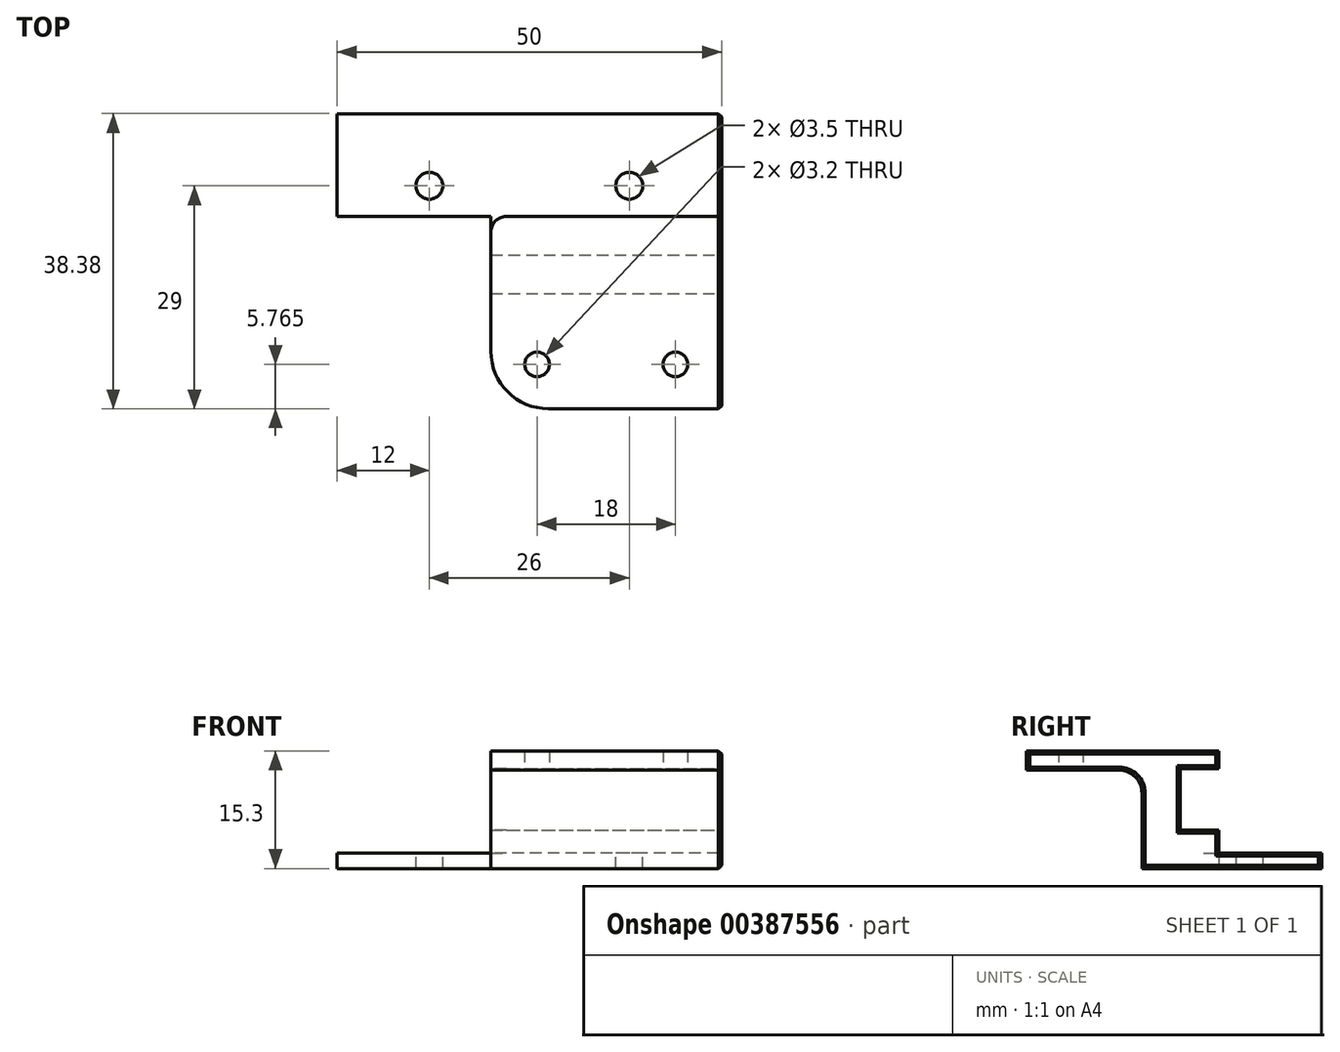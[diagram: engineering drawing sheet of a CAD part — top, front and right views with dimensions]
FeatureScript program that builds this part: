
annotation { "Feature Type Name" : "Feature", "Feature Type Description" : "" }
export const myFeature = defineFeature(function(context is Context, id is Id, definition is map)
    precondition{}
    {
        {
            var Q0;
            Q0=qCreatedBy(makeId("Right.planeOp"),FACE);
            var sketch = newSketch(context, id + "F0", { "sketchPlane" : qUnion([Q0])});
            skLineSegment(sketch, "E0", {"start": v(0, 0) * mm, "end": v(13.38, 0) * mm});
            skLineSegment(sketch, "E1", {"start": v(13.38, 0) * mm, "end": v(13.38, 2) * mm});
            skLineSegment(sketch, "E2", {"start": v(13.38, 2) * mm, "end": v(0, 2) * mm});
            skLineSegment(sketch, "E3", {"start": v(0, 2) * mm, "end": v(0, 0) * mm});
            skSolve(sketch);
        }
        {
            var Q0;
            Q0=makeQuery(id+"F0.imprint","IMPRINT",FACE,{"disambiguationData":[TD([[makeQuery(id+"F0.imprint","IMPRINT",EDGE,{"derivedFrom":sQuery(id+"F0.wireOp",EDGE,"E0")}),1.0]])]});
            extrude(context, id + "F1", {"entities" : qUnion([Q0]), "endBound" : BoundingType.SYMMETRIC, "depth" : 50 * mm});
        }
        {
            var Q0;
            Q0=makeQuery(id+"F1.opExtrude","SWEPT_FACE",FACE,{"disambiguationData":[OSD([sQuery(id+"F0.wireOp",EDGE,"E2")])]});
            var sketch = newSketch(context, id + "F2", { "sketchPlane" : qUnion([Q0])});
            skLineSegment(sketch, "E4", {"start": v(-25, 4) * mm, "end": v(25, 4) * mm, "construction": true});
            skLineSegment(sketch, "E5", {"start": v(0, 13.38) * mm, "end": v(0, 0) * mm, "construction": true});
            skCircle(sketch, "E6", {"center": v(-13, 4) * mm, "radius": 1.75 * mm});
            skCircle(sketch, "E7", {"center": v(13, 4) * mm, "radius": 1.75 * mm});
            skSolve(sketch);
        }
        {
            var Q0;
            Q0=qSketchRegion(id+"F2",true);
            extrude(context, id + "F3", {"entities" : qUnion([Q0]), "operationType" : NewBodyOperationType.REMOVE, "endBound" : BoundingType.UP_TO_NEXT, "oppositeDirection" : true, "depth" : 25 * mm});
        }
        {
            var Q0;
            Q0=makeQuery(id+"F1.opExtrude","CAP_FACE",FACE,{"disambiguationData":[OSD([sQuery(id+"F0.wireOp",EDGE,"E0"),sQuery(id+"F0.wireOp",EDGE,"E1"),sQuery(id+"F0.wireOp",EDGE,"E2"),sQuery(id+"F0.wireOp",EDGE,"E3")])],"isStart":false});
            var sketch = newSketch(context, id + "F4", { "sketchPlane" : qUnion([Q0])});
            skLineSegment(sketch, "E8", {"start": v(0, 0) * mm, "end": v(0, 15.3) * mm});
            skLineSegment(sketch, "E9", {"start": v(0, 15.3) * mm, "end": v(-25, 15.3) * mm});
            skLineSegment(sketch, "E10", {"start": v(-25, 15.3) * mm, "end": v(-25, 12.8) * mm});
            skLineSegment(sketch, "E11", {"start": v(-25, 12.8) * mm, "end": v(-10, 12.8) * mm});
            skLineSegment(sketch, "E12", {"start": v(-10, 12.8) * mm, "end": v(-10, 0) * mm});
            skLineSegment(sketch, "E13", {"start": v(-10, 0) * mm, "end": v(0, 0) * mm});
            skSolve(sketch);
        }
        {
            var Q0;
            Q0=qSketchRegion(id+"F4",true);
            extrude(context, id + "F5", {"entities" : qUnion([Q0]), "operationType" : NewBodyOperationType.ADD, "oppositeDirection" : true, "depth" : 30 * mm});
        }
        {
            var Q0;
            Q0=makeQuery(id+"F5.boolean.opBoolean","MERGE",FACE,{"derivedFrom":[makeQuery(id+"F1.opExtrude","CAP_FACE",FACE,{"disambiguationData":[OSD([sQuery(id+"F0.wireOp",EDGE,"E0"),sQuery(id+"F0.wireOp",EDGE,"E1"),sQuery(id+"F0.wireOp",EDGE,"E2"),sQuery(id+"F0.wireOp",EDGE,"E3")])],"isStart":false}),makeQuery(id+"F5.opExtrude","CAP_FACE",FACE,{"disambiguationData":[OSD([sQuery(id+"F4.wireOp",EDGE,"E8"),sQuery(id+"F4.wireOp",EDGE,"E9"),sQuery(id+"F4.wireOp",EDGE,"E10"),sQuery(id+"F4.wireOp",EDGE,"E11"),sQuery(id+"F4.wireOp",EDGE,"E12"),sQuery(id+"F4.wireOp",EDGE,"E13")])],"isStart":true})]});
            var sketch = newSketch(context, id + "F6", { "sketchPlane" : qUnion([Q0])});
            skLineSegment(sketch, "E14.bottom", {"start": v(0, 5) * mm, "end": v(-5, 5) * mm});
            skLineSegment(sketch, "E14.top", {"start": v(0, 13) * mm, "end": v(-5, 13) * mm});
            skLineSegment(sketch, "E14.left", {"start": v(0, 5) * mm, "end": v(0, 13) * mm});
            skLineSegment(sketch, "E14.right", {"start": v(-5, 5) * mm, "end": v(-5, 13) * mm});
            skSolve(sketch);
        }
        {
            var Q0;
            Q0=qSketchRegion(id+"F6",true);
            extrude(context, id + "F7", {"entities" : qUnion([Q0]), "operationType" : NewBodyOperationType.REMOVE, "endBound" : BoundingType.THROUGH_ALL, "oppositeDirection" : true, "depth" : 25 * mm});
        }
        {
            var Q0;
            Q0=makeQuery(id+"F5.opExtrude","SWEPT_FACE",FACE,{"disambiguationData":[OSD([sQuery(id+"F4.wireOp",EDGE,"E11")])]});
            var sketch = newSketch(context, id + "F8", { "sketchPlane" : qUnion([Q0])});
            skLineSegment(sketch, "E15", {"start": v(7, 25) * mm, "end": v(13, 25) * mm});
            skLineSegment(sketch, "E16", {"start": v(13, 25) * mm, "end": v(20.04, 23.1) * mm});
            skLineSegment(sketch, "E17", {"start": v(20.04, 15.37) * mm, "end": v(13, 13.47) * mm});
            skLineSegment(sketch, "E18", {"start": v(13, 13.47) * mm, "end": v(7, 13.47) * mm});
            skLineSegment(sketch, "E19", {"start": v(7, 13.47) * mm, "end": v(-0.04, 15.37) * mm});
            skLineSegment(sketch, "E20", {"start": v(-0.04, 23.1) * mm, "end": v(7, 25) * mm});
            skPoint(sketch, "E21.visualSharp", {"position": v(-14.33, 19.24) * mm});
            skArc(sketch, "E21.filletArc", {"start": v(-0.04, 23.1) * mm, "mid": v(-3, 19.24) * mm, "end": v(-0.04, 15.37) * mm});
            skPoint(sketch, "E22.visualSharp", {"position": v(34.33, 19.23) * mm});
            skArc(sketch, "E22.filletArc", {"start": v(20.04, 15.37) * mm, "mid": v(23, 19.24) * mm, "end": v(20.04, 23.1) * mm});
            skLineSegment(sketch, "E23", {"start": v(10, 13.47) * mm, "end": v(10, 25) * mm, "construction": true});
            skLineSegment(sketch, "E24", {"start": v(1, 19.24) * mm, "end": v(19, 19.24) * mm, "construction": true});
            skCircle(sketch, "E25", {"center": v(1, 19.24) * mm, "radius": 1.6 * mm});
            skCircle(sketch, "E26", {"center": v(19, 19.24) * mm, "radius": 1.6 * mm});
            skLineSegment(sketch, "E27", {"start": v(10, 25) * mm, "end": v(10, 25) * mm});
            skPoint(sketch, "E28", {"position": v(10, 19.24) * mm});
            skSolve(sketch);
        }
        {
            var Q0;
            Q0=makeQuery(id+"F8.imprint","IMPRINT",FACE,{"disambiguationData":[TD([[makeQuery(id+"F8.imprint","IMPRINT",EDGE,{"derivedFrom":sQuery(id+"F8.wireOp",EDGE,"E25")}),1.0]])]});
            var Q1;
            Q1=makeQuery(id+"F8.imprint","IMPRINT",FACE,{"disambiguationData":[TD([[makeQuery(id+"F8.imprint","IMPRINT",EDGE,{"derivedFrom":sQuery(id+"F8.wireOp",EDGE,"E26")}),1.0]])]});
            extrude(context, id + "F9", {"entities" : qUnion([Q0, Q1]), "operationType" : NewBodyOperationType.REMOVE, "endBound" : BoundingType.UP_TO_NEXT, "oppositeDirection" : true, "depth" : 25 * mm});
        }
        {
            var Q0;
            Q0=makeQuery(id+"F5.opExtrude","CAP_EDGE",EDGE,{"disambiguationData":[OSD([sQuery(id+"F4.wireOp",EDGE,"E10")])],"isStart":false});
            fillet(context, id + "F10", {"entities" : qUnion([Q0]), "radius" : 7.5 * mm, "tangentPropagation" : true, "allowEdgeOverflow" : false});
        }
        {
            var Q0;
            Q0=makeQuery(id+"F5.opExtrude","SWEPT_EDGE",EDGE,{"disambiguationData":[OSD([sQuery(id+"F4.wireOp",EDGE,"E11"),sQuery(id+"F4.wireOp",EDGE,"E12")])]});
            fillet(context, id + "F11", {"entities" : qUnion([Q0]), "radius" : 3 * mm, "tangentPropagation" : true, "allowEdgeOverflow" : false});
        }
        {
            var Q0;
            {var subQ0=sQuery(id+"F4.wireOp",EDGE,"E8");Q0=makeQuery(id+"F5.boolean.opBoolean","SPLIT",EDGE,{"disambiguationData":[topologyDisambiguationEdgeConnected([makeQuery(id+"F1.opExtrude","SWEPT_FACE",FACE,{"disambiguationData":[OSD([sQuery(id+"F0.wireOp",EDGE,"E3")])]})])],"derivedFrom":makeQuery(id+"F5.opExtrude","CAP_EDGE",EDGE,{"disambiguationData":[OSD([subQ0])],"isStart":false})});}
            fillet(context, id + "F12", {"entities" : qUnion([Q0]), "radius" : 2 * mm, "tangentPropagation" : true, "allowEdgeOverflow" : false});
        }
        {
            var Q0;
            Q0=makeQuery(id+"F5.boolean.opBoolean","MERGE",FACE,{"derivedFrom":[makeQuery(id+"F1.opExtrude","CAP_FACE",FACE,{"disambiguationData":[OSD([sQuery(id+"F0.wireOp",EDGE,"E0"),sQuery(id+"F0.wireOp",EDGE,"E1"),sQuery(id+"F0.wireOp",EDGE,"E2"),sQuery(id+"F0.wireOp",EDGE,"E3")])],"isStart":false}),makeQuery(id+"F5.opExtrude","CAP_FACE",FACE,{"disambiguationData":[OSD([sQuery(id+"F4.wireOp",EDGE,"E8"),sQuery(id+"F4.wireOp",EDGE,"E9"),sQuery(id+"F4.wireOp",EDGE,"E10"),sQuery(id+"F4.wireOp",EDGE,"E11"),sQuery(id+"F4.wireOp",EDGE,"E12"),sQuery(id+"F4.wireOp",EDGE,"E13")])],"isStart":true})]});
            chamfer(context, id + "F13", {"entities" : qUnion([Q0]), "width" : 0.4 * mm, "tangentPropagation" : true});
        }
    });
